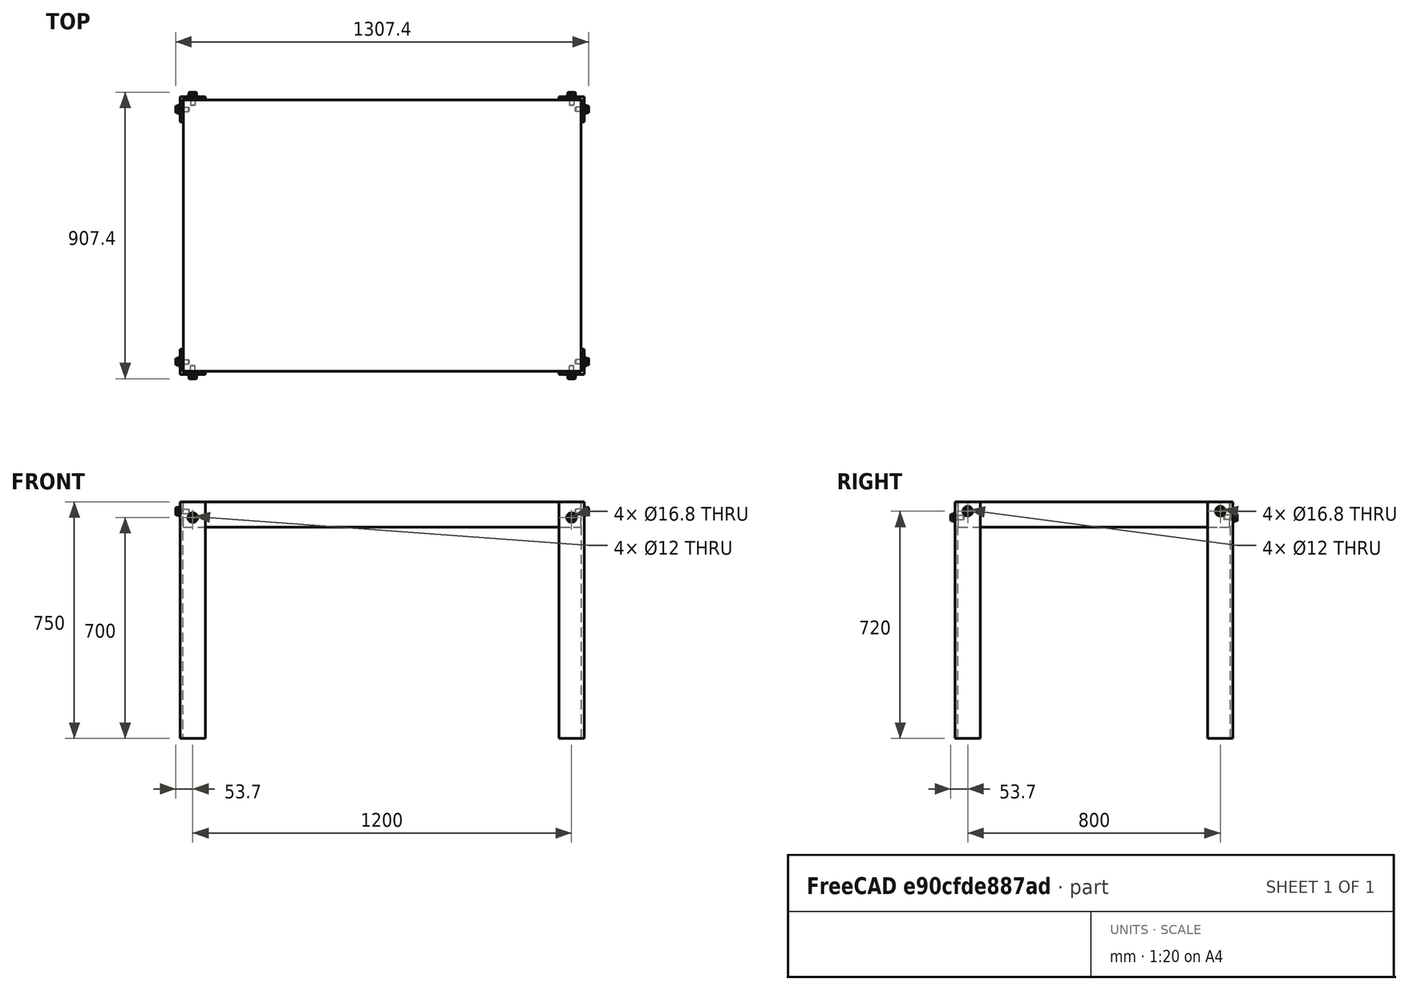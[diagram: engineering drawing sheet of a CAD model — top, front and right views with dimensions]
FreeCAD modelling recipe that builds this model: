
FCSTD DOCUMENT  (FreeCAD 0.17R13541 (Git))
Label: 201905181
License: All rights reserved
LicenseURL: http://en.wikipedia.org/wiki/All_rights_reserved
objects: Part::Cut×12, Part::Box×9, Part::FeaturePython×8, Part::Cylinder×4
note: 33 computed .brp shape members not serialized (recipe doc carries the construction recipe); baked Part::Feature solids carry a one-line shape summary decoded from their .brp

FEATURE [Part::Box] Box  label="立方体"
  AttacherType = Attacher::AttachEngine3D
  Height = 750
  Length = 80
  Width = 80
FEATURE [Part::Box] Box001  label="立方体001"
  AttacherType = Attacher::AttachEngine3D
  Height = 750
  Length = 80
  Placement = pos=(8,8,0) rot=(0,0,1;0rad)
  Width = 80
FEATURE [Part::Cut] Cut  label="Cut000"
  Base = -> Box
  Tool = -> Box001
FEATURE [Part::Box] Box002  label="立方体002"
  AttacherType = Attacher::AttachEngine3D
  Height = 750
  Length = 80
  Placement = pos=(0,800,0) rot=(0,0,1;0rad)
  Width = 80
FEATURE [Part::Box] Box003  label="立方体003"
  AttacherType = Attacher::AttachEngine3D
  Height = 750
  Length = 80
  Placement = pos=(8,792,0) rot=(0,0,1;0rad)
  Width = 80
FEATURE [Part::Box] Box004  label="立方体004"
  AttacherType = Attacher::AttachEngine3D
  Height = 750
  Length = 80
  Placement = pos=(1200,0,0) rot=(0,0,1;0rad)
  Width = 80
FEATURE [Part::Box] Box005  label="立方体005"
  AttacherType = Attacher::AttachEngine3D
  Height = 750
  Length = 80
  Placement = pos=(1192,8,0) rot=(0,0,1;0rad)
  Width = 80
FEATURE [Part::Box] Box006  label="立方体006"
  AttacherType = Attacher::AttachEngine3D
  Height = 750
  Length = 80
  Placement = pos=(1200,800,0) rot=(0,0,1;0rad)
  Width = 80
FEATURE [Part::Box] Box007  label="立方体007"
  AttacherType = Attacher::AttachEngine3D
  Height = 750
  Length = 80
  Placement = pos=(1192,792,0) rot=(0,0,1;0rad)
  Width = 80
FEATURE [Part::Cut] Cut001
  Base = -> Box002
  Tool = -> Box003
FEATURE [Part::Cut] Cut002
  Base = -> Box004
  Tool = -> Box005
FEATURE [Part::Cut] Cut003
  Base = -> Box006
  Tool = -> Box007
FEATURE [Part::Cylinder] Cylinder  label="圆柱体000"
  Angle = 360
  AttacherType = Attacher::AttachEngine3D
  Height = 1300
  Placement = pos=(-10,40,720) rot=(0,1,0;1.5708rad)
  Radius = 6
FEATURE [Part::Cylinder] Cylinder001  label="圆柱体001"
  Angle = 360
  AttacherType = Attacher::AttachEngine3D
  Height = 1300
  Placement = pos=(-10,840,720) rot=(0,1,0;1.5708rad)
  Radius = 6
FEATURE [Part::Cylinder] Cylinder002  label="圆柱体002"
  Angle = 360
  AttacherType = Attacher::AttachEngine3D
  Height = 900
  Placement = pos=(40,-10,700) rot=(-1,0,0;1.5708rad)
  Radius = 6
FEATURE [Part::Cylinder] Cylinder003  label="圆柱体003"
  Angle = 360
  AttacherType = Attacher::AttachEngine3D
  Height = 900
  Placement = pos=(1240,-10,700) rot=(-1,0,0;1.5708rad)
  Radius = 6
FEATURE [Part::Cut] Cut004
  Base = -> Cut
  Tool = -> Cylinder
FEATURE [Part::Cut] Cut005
  Base = -> Cut002
  Tool = -> Cylinder
FEATURE [Part::Cut] Cut006
  Base = -> Cut001
  Tool = -> Cylinder002
FEATURE [Part::Cut] Cut007
  Base = -> Cut004
  Tool = -> Cylinder002
FEATURE [Part::Cut] Cut008
  Base = -> Cut003
  Tool = -> Cylinder001
FEATURE [Part::Cut] Cut009
  Base = -> Cut006
  Tool = -> Cylinder001
FEATURE [Part::Cut] Cut010
  Base = -> Cut008
  Tool = -> Cylinder003
FEATURE [Part::Cut] Cut011
  Base = -> Cut005
  Tool = -> Cylinder003
FEATURE [Part::Box] Box008  label="立方体008"
  AttacherType = Attacher::AttachEngine3D
  Height = 80
  Length = 1260
  Placement = pos=(10,10,670) rot=(0,0,1;0rad)
  Width = 860
FEATURE [Part::FeaturePython] Screw  label="(M14)x30-Screw"  # Fasteners workbench fastener (typed FeaturePython)
  Placement = pos=(1282,40,720) rot=(0,1,0;1.5708rad)
  baseObject = -> Cut011 [Edge22]
  diameter = 6
  invert = false
  length = 0
  matchOuter = false
  offset = 2
  thread = false
  type = 2
FEATURE [Part::FeaturePython] Screw001  label="(M14)x30-Screw001"  # Fasteners workbench fastener (typed FeaturePython)
  Placement = pos=(1240,-2,700) rot=(1,0,0;1.5708rad)
  baseObject = -> Cut011 [Edge18]
  diameter = 6
  invert = true
  length = 0
  matchOuter = false
  offset = 2
  thread = false
  type = 2
FEATURE [Part::FeaturePython] Screw002  label="(M14)x30-Screw002"  # Fasteners workbench fastener (typed FeaturePython)
  Placement = pos=(40,-2,700) rot=(1,0,0;1.5708rad)
  baseObject = -> Cut007 [Edge9]
  diameter = 6
  invert = true
  length = 0
  matchOuter = false
  offset = 2
  thread = false
  type = 2
FEATURE [Part::FeaturePython] Screw003  label="(M14)x30-Screw003"  # Fasteners workbench fastener (typed FeaturePython)
  Placement = pos=(-2,40,720) rot=(0,-1,0;1.5708rad)
  baseObject = -> Cut007 [Edge5]
  diameter = 6
  invert = true
  length = 0
  matchOuter = false
  offset = 2
  thread = false
  type = 2
FEATURE [Part::FeaturePython] Screw004  label="(M14)x30-Screw004"  # Fasteners workbench fastener (typed FeaturePython)
  Placement = pos=(-2,840,720) rot=(0,-1,0;1.5708rad)
  baseObject = -> Cut009 [Edge5]
  diameter = 6
  invert = true
  length = 0
  matchOuter = false
  offset = 2
  thread = false
  type = 2
FEATURE [Part::FeaturePython] Screw005  label="(M14)x30-Screw005"  # Fasteners workbench fastener (typed FeaturePython)
  Placement = pos=(40,882,700) rot=(-1,0,0;1.5708rad)
  baseObject = -> Cut009 [Edge18]
  diameter = 6
  invert = false
  length = 0
  matchOuter = false
  offset = 2
  thread = false
  type = 2
FEATURE [Part::FeaturePython] Screw006  label="(M14)x30-Screw006"  # Fasteners workbench fastener (typed FeaturePython)
  Placement = pos=(1240,882,700) rot=(-1,0,0;1.5708rad)
  baseObject = -> Cut010 [Edge12]
  diameter = 6
  invert = false
  length = 0
  matchOuter = false
  offset = 2
  thread = false
  type = 2
FEATURE [Part::FeaturePython] Screw007  label="(M14)x30-Screw007"  # Fasteners workbench fastener (typed FeaturePython)
  Placement = pos=(1282,840,720) rot=(0,1,0;1.5708rad)
  baseObject = -> Cut010 [Edge20]
  diameter = 6
  invert = false
  length = 0
  matchOuter = false
  offset = 2
  thread = false
  type = 2
